# Revit family: HI-MACS_CB502
name_source: partatom
category: Appareils sanitaires
revit_build: Autodesk Revit 2015 (Build: 20140606_1530(x64)
units: mm (PartAtom-declared; Revit-internal decimal feet)

## types (1)
- HI-MACS_CB502
    Application = Bathroom (Wash basins)
    BIMobject category = Basins
    Brand url = http://www.himacs.eu
    Date of publishing = 10/20/2017
    Description DEU = Verfügbar in Alpine White S028.
Garantie: HI-MACS® 15 Jahre.
Mit und ohne Überlauf. Unterhalb montiert.

Angenehm warm in der Haptik, leicht zu pflegen: Waschbecken aus HI-MACS® sind die perfekte Lösung für jedes Traumbad. Sie werden im Gussverfahren gefertigt und sind sowohl für den flächenbündigen Einbau als auch für den Un erbau in Waschtische aus HI-MACS® bestens geeignet.
Bitte kontaktieren Sie uns, um weitere Informationen zu erhalten: www.himacs.eu
    Description ENG = Available in Alpine White S028.
Warranty: HI-MACS® 15 years.
With or without overflow. Under Mounted.
HI-MACS® Bowls offer superb ease of cleaning and a warm and pleasant feel, making them the ideal solution for creating the bathroom of your dreams. They are manufactured using a casting process and ideally suited for both flush mounting and installation into a bathroom vanity top. Visit himacs.eu for more information.
    Description ESP = Disponible en Alpine White S028.
Garantia: HI-MACS® 15 años.
Con o sin rebosadero. Encastrar.

Textura agradable y cálida, muy fácil de mantener: Los lavamanos de HI-MACS® son la solución perfecta para todo baño de ensueño. Se fabrican en el procedimiento de colado y son óptimos y adecuados tanto para instalar enrasados como también para instalar bajo encimera de HI-MACS®.
Para obtener más información, visite himacs.eu.Disponible en Alpine White S028.
Garantia: HI-MACS® 15 años.
Con o sin rebosadero. Encastrar.

Textura agradable y cálida, muy fácil de mantener: Los lavamanos de HI-MACS® son la solución perfecta para todo baño de ensueño. Se fabrican en el procedimiento de colado y son óptimos y adecuados tanto para instalar enrasados como también para instalar bajo encimera de HI-MACS®.
Para obtener más información, visite himacs.eu.
    Description ITA = Disponibile in Alpine White S028.
Garanzia: HI-MACS® 15 anni.
Con o senza troppopieno. Installazione a filo al di sotto dei top.

Le vaschette HI-MACS® garantiscono facilità di impiego per la pulizia nonché un appeal caldo e autentico, facendone la soluzione ideale per dare vita a una zona bagno da sogno. Essi vengono prodotti mediante il processo di stampaggio e sono ideali sia per strutture con rubinetteria a sé sia per integrazione in un piano completo da bagno.
Per maggiori informazioni visitate il nostro sito internet himacs.eu 
Disponibile in Alpine White S028.
Garanzia: HI-MACS® 15 anni.
Con o senza troppopieno. Installazione a filo al di sotto dei top.

Le vaschette HI-MACS® garantiscono facilità di impiego per la pulizia nonché un appeal caldo e autentico, facendone la soluzione ideale per dare vita a una zona bagno da sogno. Essi vengono prodotti mediante il processo di stampaggio e sono ideali sia per strutture con rubinetteria a sé sia per integrazione in un piano completo da bagno.
Per maggiori informazioni visitate il nostro sito internet himacs.eu
    Design country = Italy
    Edition number = 1
    Elévation par défaut = 1219 mm
    Fabricant = HI-MACS
    Heigth = 120 mm  [stored 0.393701 ft]
    IFC Classification = Furnishing Element
    Length = 500 mm  [stored 1.64042 ft]
    Manufacturer country = Italy
    Manufacturer name = HI-MACS®
    Material main = Solid surface
    Material secondary = Natural Acrylic Stone
    Modèle = CB 502
    Mounting = Under Mounted
    NBS Reference Code = 35-65-70-94
    NBS Reference Description = Wash Basin Systems
    Nominal height = 280 mm  [stored 0.918635 ft]
    Nominal width = 500 mm  [stored 1.64042 ft]
    Product Guid = 029f7d3f-78c2-46d4-82dd-6a03a4c6124e
    Product SKU = CB502
    Product certification = http://himacs.eu
    Product data url = https://bimobject.com
    Product family = Sinks, Baby Baths & Bowls
    Product group = Bowls
    Product url = http://himacs.eu
    QR code = http://bimobject.com
    Technical description = http://himacs.eu
    UNSPSC Code = 301815
    URL = http://himacs.eu
    Uniclass 1.4 Code = L7212
    Uniclass 1.4 Description = Washbasins
    Uniclass 2.0 Code = SS-35-65-70-94
    Uniclass 2.0 Description = Wash Basin Systems
    WASHBASIN MATERIAL = HI-MACS Natural Acrylic Stone
    Weight Net (Kg) = 6.3
    Weigth KG = 6.3
    Width = 280 mm  [stored 0.918635 ft]
    Youtube clip = https://www.youtube.com

note: [stored X ft] marks values corroborated as IEEE doubles in the binary element streams (Revit-internal decimal feet)
